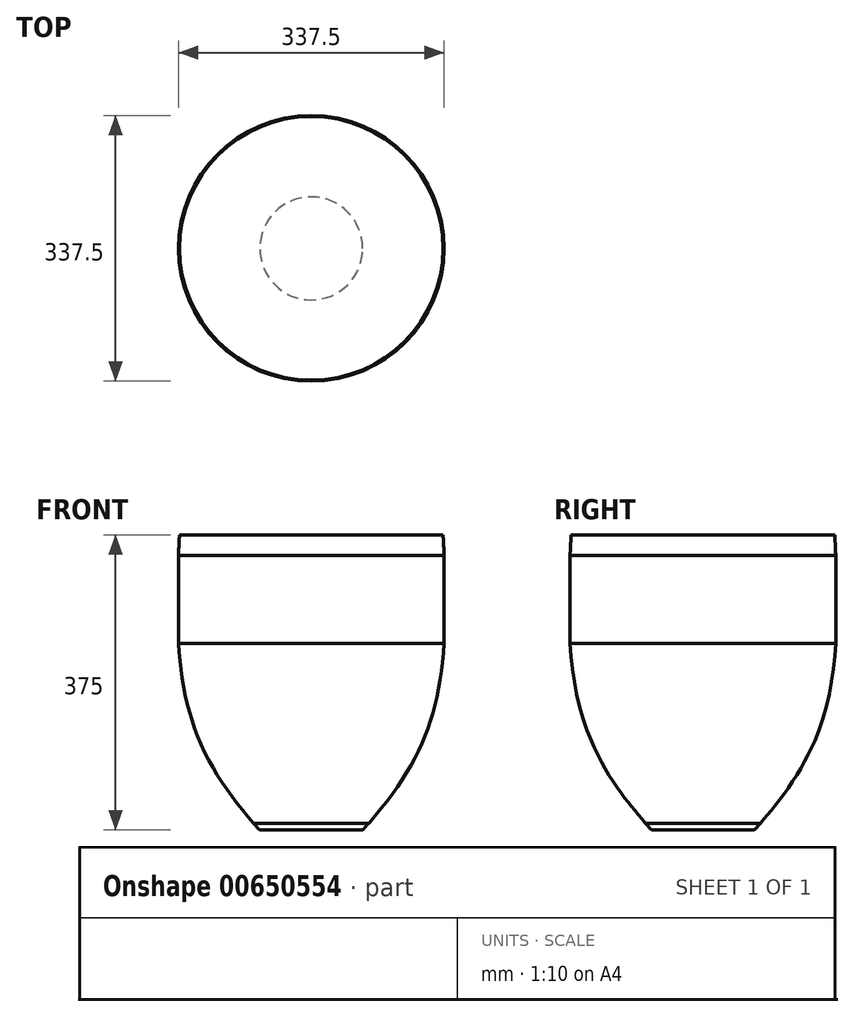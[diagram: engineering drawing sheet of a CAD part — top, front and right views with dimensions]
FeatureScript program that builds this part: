
annotation { "Feature Type Name" : "Feature", "Feature Type Description" : "" }
export const myFeature = defineFeature(function(context is Context, id is Id, definition is map)
    precondition{}
    {
        {
            var Q0;
            Q0=qCreatedBy(makeId("Top.planeOp"),FACE);
            var sketch = newSketch(context, id + "F0", { "sketchPlane" : qUnion([Q0])});
            skCircle(sketch, "E0", {"center": v(0, 0) * mm, "radius": 225 * mm});
            skSolve(sketch);
        }
        {
            var Q0;
            Q0 = qSketchRegion(id + "F0", true);
            extrude(context, id + "F1", {"entities" : qUnion([Q0]), "depth" : 500 * mm, "offsetDistance" : 25 * mm});
        }
        {
            var Q0;
            Q0=qCreatedBy(makeId("Front.planeOp"),FACE);
            var sketch = newSketch(context, id + "F2", { "sketchPlane" : qUnion([Q0])});
            skFitSpline(sketch, "E1", {"points": [v(-87.18, 0) * mm, v(-222.65, 509.98) * mm], "startDerivative": vector(-395.6, 432.93) * mm, "endDerivative": vector(44.99, 764.75) * mm});
            skLineSegment(sketch, "E2", {"start": v(-87.18, 0) * mm, "end": v(-370.36, 0) * mm});
            skLineSegment(sketch, "E3", {"start": v(-370.36, 0) * mm, "end": v(-370.36, 526.2) * mm});
            skLineSegment(sketch, "E4", {"start": v(-370.36, 526.2) * mm, "end": v(-222.65, 509.98) * mm});
            skLineSegment(sketch, "E5", {"start": v(-97.42, 11.4) * mm, "end": v(-87.18, 0) * mm});
            skSolve(sketch);
        }
        {
            var Q0;
            Q0=qCreatedBy(makeId("Front.planeOp"),FACE);
            var sketch = newSketch(context, id + "F3", { "sketchPlane" : qUnion([Q0])});
            skLineSegment(sketch, "E6", {"start": v(0, 0) * mm, "end": v(0, 627.1) * mm, "construction": true});
            skSolve(sketch);
        }
        {
            var Q0;
            Q0 = qSketchRegion(id + "F2", true);
            var Q1;
            Q1=sQuery(id+"F3.wireOp",EDGE,"E6");
            revolve(context, id + "F4", {"operationType" : NewBodyOperationType.REMOVE, "entities" : qUnion([Q0]), "axis" : qUnion([Q1]), "revolveType" : RevolveType.FULL, "oppositeDirection" : true});
        }
        {
            var Q0;
            Q0=makeQuery(id+"F1.opExtrude","SWEPT_BODY",BODY,{"disambiguationData":[OSD([sQuery(id+"F0.wireOp",EDGE,"E0")])]});
            var Q1;
            Q1=qCreatedBy(makeId("Origin.pointOp"),VERTEX);
            transform(context, id + "F5", {"entities" : qUnion([Q0]), "transformType" : TransformType.SCALE_UNIFORMLY, "scale" : 0.75, "scalePoint" : qUnion([Q1]), "makeCopy" : false});
        }
    });
